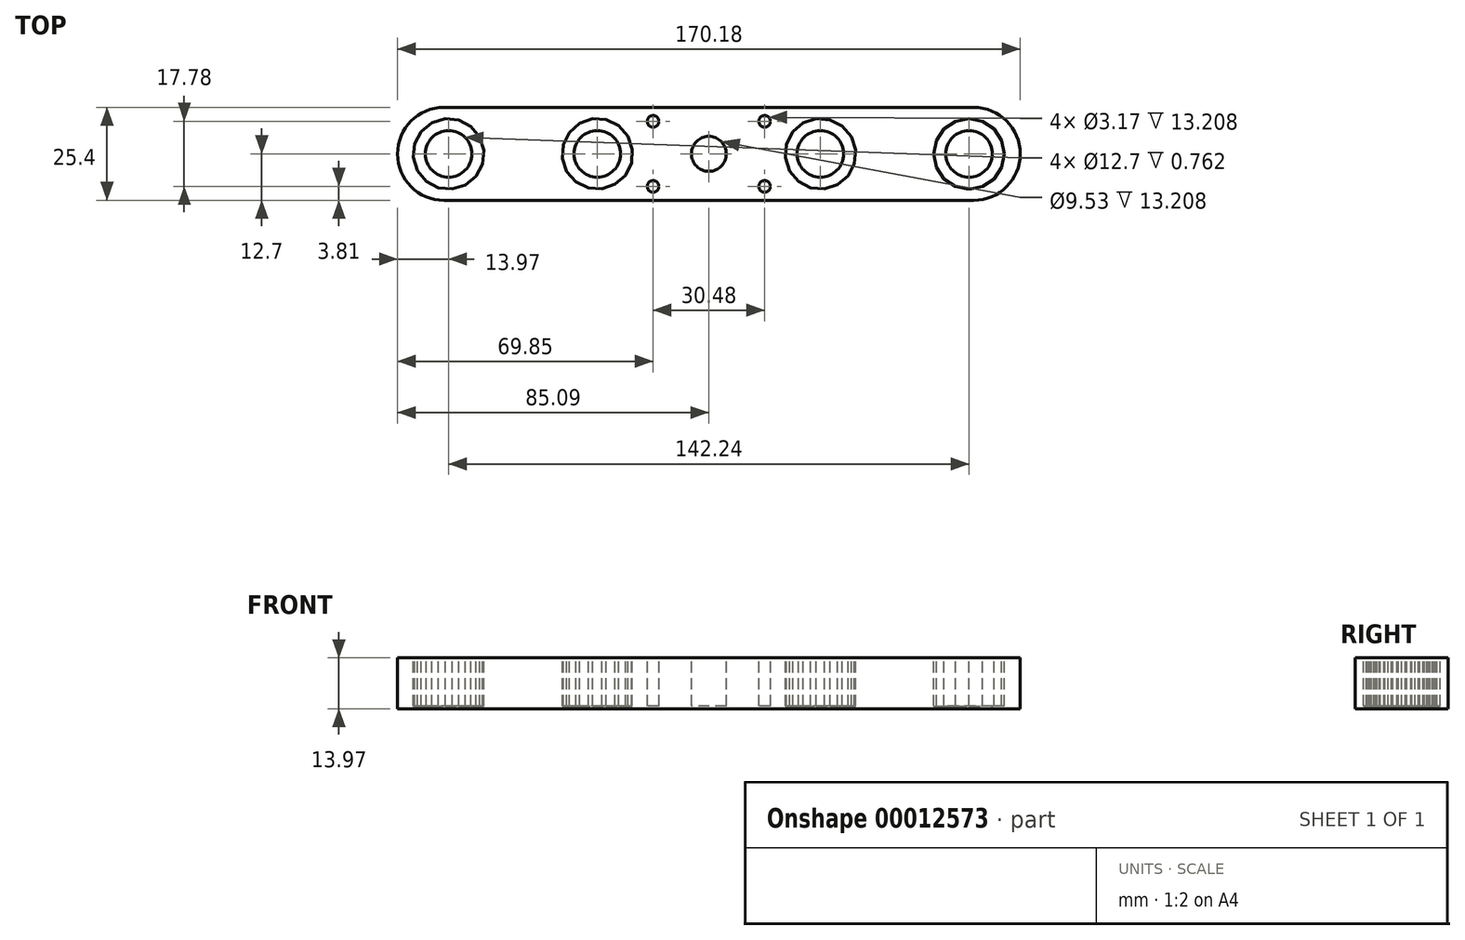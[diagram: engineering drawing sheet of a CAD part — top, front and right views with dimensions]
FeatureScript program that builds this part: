
annotation { "Feature Type Name" : "Feature", "Feature Type Description" : "" }
export const myFeature = defineFeature(function(context is Context, id is Id, definition is map)
    precondition{}
    {
        {
            var Q0;
            Q0=qCreatedBy(makeId("Top.planeOp"),FACE);
            var sketch = newSketch(context, id + "F0", { "sketchPlane" : qUnion([Q0])});
            skLineSegment(sketch, "E0.rect.bottom", {"start": v(-85.1, 12.7) * mm, "end": v(85.1, 12.7) * mm});
            skLineSegment(sketch, "E0.rect.top", {"start": v(-85.1, -12.7) * mm, "end": v(85.1, -12.7) * mm});
            skLineSegment(sketch, "E0.rect.left", {"start": v(-85.1, 12.7) * mm, "end": v(-85.1, -12.7) * mm});
            skLineSegment(sketch, "E0.rect.right", {"start": v(85.1, 12.7) * mm, "end": v(85.1, -12.7) * mm});
            skPoint(sketch, "E0.rect.middle", {"position": v(0, 0) * mm});
            skSolve(sketch);
        }
        {
            var Q0;
            Q0 = qSketchRegion(id + "F0", true);
            extrude(context, id + "F1", {"entities" : qUnion([Q0]), "depth" : 13.97 * mm});
        }
        {
            var Q0;
            Q0=makeQuery(id+"F1.opExtrude","SWEPT_EDGE",EDGE,{"disambiguationData":[OSD([sQuery(id+"F0.wireOp",EDGE,"E0.rect.bottom"),sQuery(id+"F0.wireOp",EDGE,"E0.rect.left")])]});
            var Q1;
            Q1=makeQuery(id+"F1.opExtrude","SWEPT_EDGE",EDGE,{"disambiguationData":[OSD([sQuery(id+"F0.wireOp",EDGE,"E0.rect.bottom"),sQuery(id+"F0.wireOp",EDGE,"E0.rect.right")])]});
            var Q2;
            Q2=makeQuery(id+"F1.opExtrude","SWEPT_EDGE",EDGE,{"disambiguationData":[OSD([sQuery(id+"F0.wireOp",EDGE,"E0.rect.top"),sQuery(id+"F0.wireOp",EDGE,"E0.rect.right")])]});
            var Q3;
            Q3=makeQuery(id+"F1.opExtrude","SWEPT_EDGE",EDGE,{"disambiguationData":[OSD([sQuery(id+"F0.wireOp",EDGE,"E0.rect.top"),sQuery(id+"F0.wireOp",EDGE,"E0.rect.left")])]});
            fillet(context, id + "F2", {"entities" : qUnion([Q0, Q1, Q2, Q3]), "radius" : 12.7 * mm, "tangentPropagation" : true, "allowEdgeOverflow" : false});
        }
        {
            var Q0;
            Q0=makeQuery(id+"F1.opExtrude","CAP_FACE",FACE,{"disambiguationData":[OSD([sQuery(id+"F0.wireOp",EDGE,"E0.rect.bottom"),sQuery(id+"F0.wireOp",EDGE,"E0.rect.top"),sQuery(id+"F0.wireOp",EDGE,"E0.rect.left"),sQuery(id+"F0.wireOp",EDGE,"E0.rect.right")])],"isStart":false});
            var sketch = newSketch(context, id + "F3", { "sketchPlane" : qUnion([Q0])});
            skLineSegment(sketch, "E1.rect.bottom", {"start": v(-15.24, 8.9) * mm, "end": v(15.24, 8.9) * mm, "construction": true});
            skLineSegment(sketch, "E1.rect.top", {"start": v(-15.24, -8.9) * mm, "end": v(15.24, -8.9) * mm, "construction": true});
            skLineSegment(sketch, "E1.rect.left", {"start": v(-15.24, 8.9) * mm, "end": v(-15.24, -8.9) * mm, "construction": true});
            skLineSegment(sketch, "E1.rect.right", {"start": v(15.24, 8.9) * mm, "end": v(15.24, -8.9) * mm, "construction": true});
            skPoint(sketch, "E1.rect.middle", {"position": v(0, 0) * mm});
            skCircle(sketch, "E2", {"center": v(-15.24, 8.9) * mm, "radius": 1.59 * mm});
            skCircle(sketch, "E3", {"center": v(15.24, 8.9) * mm, "radius": 1.59 * mm});
            skCircle(sketch, "E4", {"center": v(15.24, -8.9) * mm, "radius": 1.59 * mm});
            skCircle(sketch, "E5", {"center": v(-15.24, -8.9) * mm, "radius": 1.59 * mm});
            skCircle(sketch, "E6", {"center": v(0, 0) * mm, "radius": 4.76 * mm});
            skCircle(sketch, "E7.cCircle", {"center": v(-71.12, 0) * mm, "radius": 9.65 * mm, "construction": true});
            skLineSegment(sketch, "E7.0", {"start": v(-72.07, 9.6) * mm, "end": v(-68.32, 9.24) * mm});
            skLineSegment(sketch, "E7.1", {"start": v(-68.32, 9.24) * mm, "end": v(-65, 7.46) * mm});
            skLineSegment(sketch, "E7.2", {"start": v(-65, 7.46) * mm, "end": v(-62.61, 4.55) * mm});
            skLineSegment(sketch, "E7.3", {"start": v(-62.61, 4.55) * mm, "end": v(-61.52, 0.95) * mm});
            skLineSegment(sketch, "E7.4", {"start": v(-61.52, 0.95) * mm, "end": v(-61.88, -2.8) * mm});
            skLineSegment(sketch, "E7.5", {"start": v(-61.88, -2.8) * mm, "end": v(-63.66, -6.12) * mm});
            skLineSegment(sketch, "E7.6", {"start": v(-63.66, -6.12) * mm, "end": v(-66.57, -8.5) * mm});
            skLineSegment(sketch, "E7.7", {"start": v(-66.57, -8.5) * mm, "end": v(-70.17, -9.6) * mm});
            skLineSegment(sketch, "E7.8", {"start": v(-70.17, -9.6) * mm, "end": v(-73.92, -9.24) * mm});
            skLineSegment(sketch, "E7.9", {"start": v(-73.92, -9.24) * mm, "end": v(-77.24, -7.46) * mm});
            skLineSegment(sketch, "E7.10", {"start": v(-77.24, -7.46) * mm, "end": v(-79.63, -4.55) * mm});
            skLineSegment(sketch, "E7.11", {"start": v(-79.63, -4.55) * mm, "end": v(-80.72, -0.95) * mm});
            skLineSegment(sketch, "E7.12", {"start": v(-80.72, -0.95) * mm, "end": v(-80.36, 2.8) * mm});
            skLineSegment(sketch, "E7.13", {"start": v(-80.36, 2.8) * mm, "end": v(-78.58, 6.12) * mm});
            skLineSegment(sketch, "E7.14", {"start": v(-78.58, 6.12) * mm, "end": v(-75.67, 8.5) * mm});
            skLineSegment(sketch, "E7.15", {"start": v(-75.67, 8.5) * mm, "end": v(-72.07, 9.6) * mm});
            skCircle(sketch, "E8.cCircle", {"center": v(-30.48, 0) * mm, "radius": 9.65 * mm, "construction": true});
            skLineSegment(sketch, "E8.0", {"start": v(-31.78, 9.56) * mm, "end": v(-28.02, 9.33) * mm});
            skLineSegment(sketch, "E8.1", {"start": v(-28.02, 9.33) * mm, "end": v(-24.64, 7.68) * mm});
            skLineSegment(sketch, "E8.2", {"start": v(-24.64, 7.68) * mm, "end": v(-22.14, 4.86) * mm});
            skLineSegment(sketch, "E8.3", {"start": v(-22.14, 4.86) * mm, "end": v(-20.92, 1.3) * mm});
            skLineSegment(sketch, "E8.4", {"start": v(-20.92, 1.3) * mm, "end": v(-21.15, -2.46) * mm});
            skLineSegment(sketch, "E8.5", {"start": v(-21.15, -2.46) * mm, "end": v(-22.8, -5.84) * mm});
            skLineSegment(sketch, "E8.6", {"start": v(-22.8, -5.84) * mm, "end": v(-25.62, -8.34) * mm});
            skLineSegment(sketch, "E8.7", {"start": v(-25.62, -8.34) * mm, "end": v(-29.18, -9.56) * mm});
            skLineSegment(sketch, "E8.8", {"start": v(-29.18, -9.56) * mm, "end": v(-32.94, -9.33) * mm});
            skLineSegment(sketch, "E8.9", {"start": v(-32.94, -9.33) * mm, "end": v(-36.32, -7.68) * mm});
            skLineSegment(sketch, "E8.10", {"start": v(-36.32, -7.68) * mm, "end": v(-38.82, -4.86) * mm});
            skLineSegment(sketch, "E8.11", {"start": v(-38.82, -4.86) * mm, "end": v(-40.04, -1.3) * mm});
            skLineSegment(sketch, "E8.12", {"start": v(-40.04, -1.3) * mm, "end": v(-39.81, 2.46) * mm});
            skLineSegment(sketch, "E8.13", {"start": v(-39.81, 2.46) * mm, "end": v(-38.16, 5.84) * mm});
            skLineSegment(sketch, "E8.14", {"start": v(-38.16, 5.84) * mm, "end": v(-35.34, 8.34) * mm});
            skLineSegment(sketch, "E8.15", {"start": v(-35.34, 8.34) * mm, "end": v(-31.78, 9.56) * mm});
            skCircle(sketch, "E9.cCircle", {"center": v(30.48, 0) * mm, "radius": 9.65 * mm, "construction": true});
            skLineSegment(sketch, "E9.0", {"start": v(29.4, 9.6) * mm, "end": v(33.14, 9.28) * mm});
            skLineSegment(sketch, "E9.1", {"start": v(33.14, 9.28) * mm, "end": v(36.5, 7.55) * mm});
            skLineSegment(sketch, "E9.2", {"start": v(36.5, 7.55) * mm, "end": v(38.92, 4.68) * mm});
            skLineSegment(sketch, "E9.3", {"start": v(38.92, 4.68) * mm, "end": v(40.07, 1.09) * mm});
            skLineSegment(sketch, "E9.4", {"start": v(40.07, 1.09) * mm, "end": v(39.76, -2.66) * mm});
            skLineSegment(sketch, "E9.5", {"start": v(39.76, -2.66) * mm, "end": v(38.03, -6.01) * mm});
            skLineSegment(sketch, "E9.6", {"start": v(38.03, -6.01) * mm, "end": v(35.16, -8.44) * mm});
            skLineSegment(sketch, "E9.7", {"start": v(35.16, -8.44) * mm, "end": v(31.57, -9.6) * mm});
            skLineSegment(sketch, "E9.8", {"start": v(31.57, -9.6) * mm, "end": v(27.82, -9.28) * mm});
            skLineSegment(sketch, "E9.9", {"start": v(27.82, -9.28) * mm, "end": v(24.47, -7.55) * mm});
            skLineSegment(sketch, "E9.10", {"start": v(24.47, -7.55) * mm, "end": v(22.04, -4.68) * mm});
            skLineSegment(sketch, "E9.11", {"start": v(22.04, -4.68) * mm, "end": v(20.89, -1.09) * mm});
            skLineSegment(sketch, "E9.12", {"start": v(20.89, -1.09) * mm, "end": v(21.2, 2.66) * mm});
            skLineSegment(sketch, "E9.13", {"start": v(21.2, 2.66) * mm, "end": v(22.93, 6.01) * mm});
            skLineSegment(sketch, "E9.14", {"start": v(22.93, 6.01) * mm, "end": v(25.8, 8.44) * mm});
            skLineSegment(sketch, "E9.15", {"start": v(25.8, 8.44) * mm, "end": v(29.4, 9.6) * mm});
            skCircle(sketch, "E10.cCircle", {"center": v(71.12, 0) * mm, "radius": 9.65 * mm, "construction": true});
            skLineSegment(sketch, "E10.0", {"start": v(71.12, 9.65) * mm, "end": v(74.81, 8.92) * mm});
            skLineSegment(sketch, "E10.1", {"start": v(74.81, 8.92) * mm, "end": v(77.94, 6.82) * mm});
            skLineSegment(sketch, "E10.2", {"start": v(77.94, 6.82) * mm, "end": v(80.04, 3.7) * mm});
            skLineSegment(sketch, "E10.3", {"start": v(80.04, 3.7) * mm, "end": v(80.77, 0) * mm});
            skLineSegment(sketch, "E10.4", {"start": v(80.77, 0) * mm, "end": v(80.04, -3.7) * mm});
            skLineSegment(sketch, "E10.5", {"start": v(80.04, -3.7) * mm, "end": v(77.94, -6.82) * mm});
            skLineSegment(sketch, "E10.6", {"start": v(77.94, -6.82) * mm, "end": v(74.81, -8.92) * mm});
            skLineSegment(sketch, "E10.7", {"start": v(74.81, -8.92) * mm, "end": v(71.12, -9.65) * mm});
            skLineSegment(sketch, "E10.8", {"start": v(71.12, -9.65) * mm, "end": v(67.43, -8.92) * mm});
            skLineSegment(sketch, "E10.9", {"start": v(67.43, -8.92) * mm, "end": v(64.3, -6.82) * mm});
            skLineSegment(sketch, "E10.10", {"start": v(64.3, -6.82) * mm, "end": v(62.2, -3.7) * mm});
            skLineSegment(sketch, "E10.11", {"start": v(62.2, -3.7) * mm, "end": v(61.47, 0) * mm});
            skLineSegment(sketch, "E10.12", {"start": v(61.47, 0) * mm, "end": v(62.2, 3.7) * mm});
            skLineSegment(sketch, "E10.13", {"start": v(62.2, 3.7) * mm, "end": v(64.3, 6.82) * mm});
            skLineSegment(sketch, "E10.14", {"start": v(64.3, 6.82) * mm, "end": v(67.43, 8.92) * mm});
            skLineSegment(sketch, "E10.15", {"start": v(67.43, 8.92) * mm, "end": v(71.12, 9.65) * mm});
            skSolve(sketch);
        }
        {
            var Q0;
            Q0 = qSketchRegion(id + "F3", true);
            extrude(context, id + "F4", {"entities" : qUnion([Q0]), "operationType" : NewBodyOperationType.REMOVE, "oppositeDirection" : true, "depth" : 13.2 * mm});
        }
        {
            var Q0;
            Q0=makeQuery(id+"F1.opExtrude","CAP_FACE",FACE,{"disambiguationData":[OSD([sQuery(id+"F0.wireOp",EDGE,"E0.rect.bottom"),sQuery(id+"F0.wireOp",EDGE,"E0.rect.top"),sQuery(id+"F0.wireOp",EDGE,"E0.rect.left"),sQuery(id+"F0.wireOp",EDGE,"E0.rect.right")])],"isStart":false});
            var sketch = newSketch(context, id + "F5", { "sketchPlane" : qUnion([Q0])});
            skCircle(sketch, "E11", {"center": v(-71.12, 0) * mm, "radius": 6.35 * mm});
            skCircle(sketch, "E12", {"center": v(-30.48, 0) * mm, "radius": 6.35 * mm});
            skCircle(sketch, "E13", {"center": v(30.48, 0) * mm, "radius": 6.35 * mm});
            skCircle(sketch, "E14", {"center": v(71.12, 0) * mm, "radius": 6.35 * mm});
            skSolve(sketch);
        }
        {
            var Q0;
            Q0 = qSketchRegion(id + "F5", true);
            extrude(context, id + "F6", {"entities" : qUnion([Q0]), "operationType" : NewBodyOperationType.REMOVE, "oppositeDirection" : true, "depth" : 25.4 * mm});
        }
    });
